# Revit family: Gira_210427
name_source: partatom
category: Elektroinstallationen
revit_build: Autodesk Revit 2017 (Build: 20160225_1515(x64)
units: mm (PartAtom-declared; Revit-internal decimal feet)

## family parameters
Basisbauteil = Fläche
Beim Laden mit Abzugskörper schneiden = Nein
Bemaßung runder Anschluss = Durchmesser verwenden
Beschriftungsausrichtung beibehalten = Nein
Gemeinsam genutzt = Nein
Raumberechnungspunkt = Nein
Teiletyp = Normal

## types (1)
- Gira_210427
    Akustisches Signal = Ja
    Analogeingang = Nein
    Andere Bussysteme = ohne
    Ausführung = CO2-Sensor
    BIM = https://media.stage.bim.site und Tasten.rfa
    Bauelement = Sys55_Abdeckung_Schalten und Tasten
    Beschreibung = KNX CO2-Sensor mit Luftfeuchte- und Raumtemperaturregler System 55 Reinweiß seidenmatt CO?-Sensor mit einer integrierten KNX Busankopplung und zwei Binäreingängen zum Messen der Kohlendioxid-Konzentration, relativen Luftfeuchte und Raumtemperatur.  Merkmale: - Grenzwertüberwachung für CO2-Konzentration und Luftfeuchte. - Taupunktalarmierung für z. B. Kühldecken und Wintergärten, zur Vermeidung möglicher Schimmelbildung. - Zwei Binäreingänge zum Anschluss potenzialfreier Kontakte. - Logikgatter für einfache Verknüpfungsfunktionen. Sensor: - Beim CO2-Sensor sind maximal vier unterschiedliche Grenzwerte einstellbar. - Anpassung an aktuelle Ortshöhe über NN. - Beim Feuchtesensor sind max. zwei Grenzwerte einstellbar. Regler: - 5 Betriebsarten: Komfort, Stand-by, Nacht, Frost- bzw. Hitzeschutz und Reglersperre (z. B. Taupunkt-Betrieb). - Heiz-  Kühlfunktionen: Heizen, Kühlen, Heizen und Kühlen, Grund- und Zusatzheizen, Grund- und Zusatzkühlen. - Voreingestellte Regelparameter für gängige Heiz- bzw. Kühlkörper. - Regler abschaltbar (Taupunktbetrieb) bzw. Regler oder Bedienung des Reglers sperrbar. - Ventilschutzfunktion (Ventil wird zyklisch alle 24 Stunden geöffnet). - Regelungsarten: stetige PI-Regelung, schaltende PI-Regelung (PWM) und schaltende 2-Punkt-Regelung (Ein Aus). Eingänge: - Freie Zuordnung der Funktionen Schalten, Dimmen, Jalousie und Wertgeber zu den Eingängen. - Sperrobjekt zum Sperren einzelner Eingänge. - Verhalten bei Busspannungswiederkehr parametrierbar. - Telegrammratenbegrenzung. - Funktion Schalten: zwei unabhängige Schaltobjekte für jeden Eingang vorhanden und einzeln freischaltbar, Befehl bei steigender und fallender Flanke unabhängig einstellbar (EIN, AUS, UM, keine Reaktion). - Funktion Dimmen: Einflächen- und Zweiflächenbedienung, Zeit zwischen Dimmen und Schalten und Dimmschrittweite einstellbar, Telegramm-Wiederholung und Stopp-Telegramm senden möglich. - Funktion Jalousie: Befehl bei steigender Flanke einstellbar (keine Funktion, AUF, AB, UM), Bedienkonzept parametrierbar, Zeit zwischen Kurz- und Langzeitbetrieb einstellbar, Lamellenverstellzeit einstellbar. - Funktion Wertgeber und Lichtszenennebenstelle: Flanke (Taster als Schließer, Taster als Öffner, Schalter) und Wert bei Flanke parametrierbar, Wertverstellung bei Taster über langen Tastendruck für Wertgeber möglich, Lichtszenennebenstelle mit bzw. ohne Speicherfunktion.  Hinweise : - Der CO2-Sensor besitzt keine Bedien- oder Anzeigeelemente. - Bei Anschluss der externen Eingänge wird die Verwendung einer Schalterklemmdose empfohlen. - Zum Betrieb des CO2-Sensors ist kein separater Busankoppler notwendig.
    Bussystem Funkbus = Nein
    Bussystem KNX = Ja
    Bussystem KNX-Funk = Nein
    Bussystem LON = Nein
    Bussystem Powernet = Nein
    Datenblatt = https://katalog.gira.de
    Farbe = weiß
    GTIN = 4010337084495
    HAN = 210427
    Hersteller = Gira
    Mit Busankopplung = Nein
    Mit DCF77 = Nein
    Mit Heizung = Nein
    Montageart = Unterputz
    Produktseite = http://katalog.gira.de
    RAL-Nummer (ähnlich) = 9010
    Schutzart (IP) = IP20
    Typname = KNX CO?-Sensor Luftfeuchteregler + RTR System 55 Reinweiß m
    URL = https://www.gira.de
    Vorgabe-Ansicht = 1219 mm
    Wetterstation = Nein

## geometry (parser evidence)
native form markers: Sweep x6
no freeform markers — native parametric forms only
